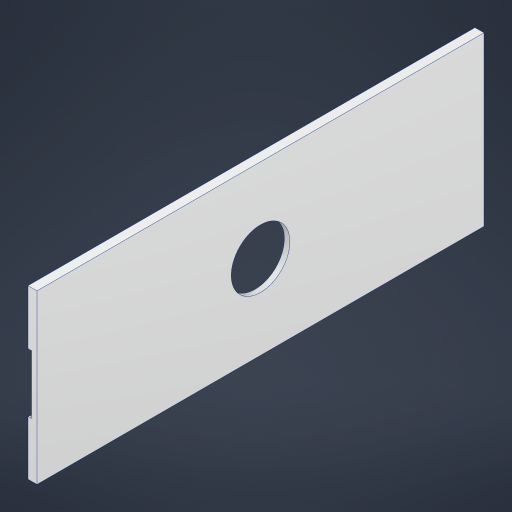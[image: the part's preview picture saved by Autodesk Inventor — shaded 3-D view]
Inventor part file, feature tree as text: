
AUTODESK INVENTOR PART (.ipt)
format: ipt  version: 2024 (Build 280153000, 153)  size: 199,168 bytes
history: native  units: mm
features: extrude x3, sketch x3, projected_geometry x1
ambient origin geometry x8: Origin, YZ Plane, XZ Plane, XY Plane, X Axis, Y Axis, Z Axis, Center Point
bodies: Solid1 (feature_tree)
feature tree (7):
  extrude  "Extrusion1"  Depth=496.0mm
  extrude  "Extrusion5"  Depth=186.0mm
  extrude  "Extrusion6"  Depth=93.0mm
  sketch  "Sketch1"  dims[d0=10.0mm d1=496.0mm]
  sketch  "Sketch3"  dims[d2=186.0mm d3=0.0mm d16=65.0mm]
  projected_geometry  "Projected Loop1"
  sketch  "Sketch5"  dims[d17=186.0mm d18=0.0mm d19=93.0mm d20=248.0mm d21=248.0mm d22=93.0mm d23=181.0mm d24=4.0mm d25=0.0mm]
